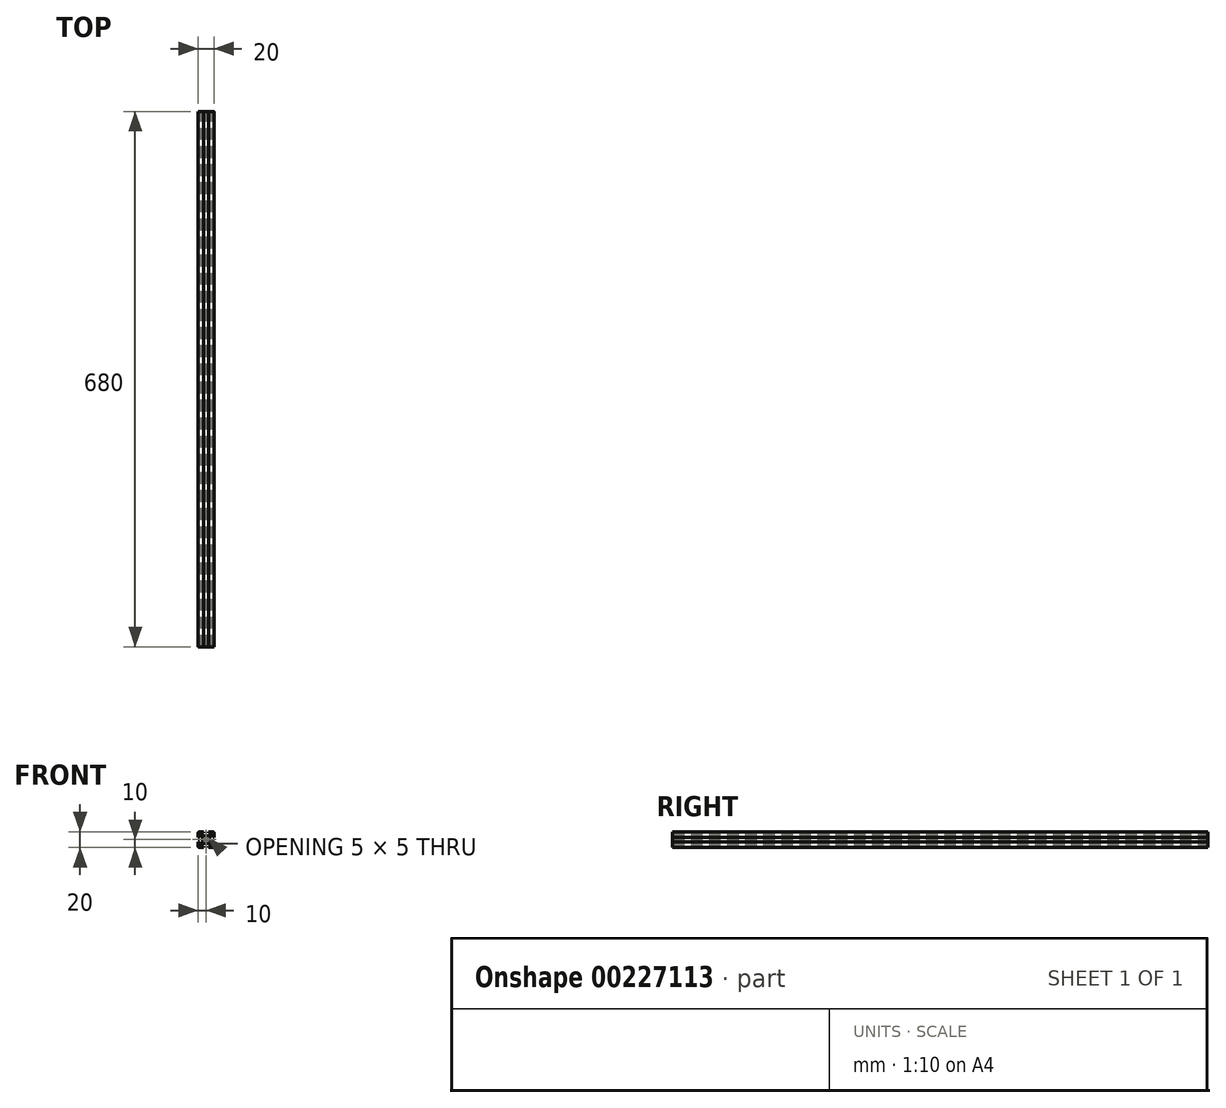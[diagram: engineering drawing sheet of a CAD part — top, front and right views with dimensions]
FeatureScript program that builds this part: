
annotation { "Feature Type Name" : "Feature", "Feature Type Description" : "" }
export const myFeature = defineFeature(function(context is Context, id is Id, definition is map)
    precondition{}
    {
        {
            var Q0;
            Q0=qCreatedBy(makeId("Front.planeOp"),FACE);
            var sketch = newSketch(context, id + "F0", { "sketchPlane" : qUnion([Q0])});
            skLineSegment(sketch, "E0.bottom", {"start": v(8.5, -10) * mm, "end": v(3, -10) * mm});
            skLineSegment(sketch, "E0.top", {"start": v(8.5, 10) * mm, "end": v(3, 10) * mm});
            skLineSegment(sketch, "E0.left", {"start": v(10, -8.5) * mm, "end": v(10, -3) * mm});
            skLineSegment(sketch, "E0.right", {"start": v(-10, -8.5) * mm, "end": v(-10, -3) * mm});
            skPoint(sketch, "E0.middle", {"position": v(0, 0) * mm});
            skLineSegment(sketch, "E1.bottom", {"start": v(6, -8.5) * mm, "end": v(3, -8.5) * mm});
            skLineSegment(sketch, "E1.top", {"start": v(6, 8.5) * mm, "end": v(3, 8.5) * mm});
            skLineSegment(sketch, "E1.left", {"start": v(8.5, -6) * mm, "end": v(8.5, -3) * mm});
            skLineSegment(sketch, "E1.right", {"start": v(-8.5, -6) * mm, "end": v(-8.5, -3) * mm});
            skLineSegment(sketch, "E2.bottom", {"start": v(3.44, -4.5) * mm, "end": v(-3.44, -4.5) * mm});
            skLineSegment(sketch, "E2.top", {"start": v(3.44, 4.5) * mm, "end": v(-3.44, 4.5) * mm});
            skLineSegment(sketch, "E2.left", {"start": v(4.5, -3.44) * mm, "end": v(4.5, 3.44) * mm});
            skLineSegment(sketch, "E2.right", {"start": v(-4.5, -3.44) * mm, "end": v(-4.5, 3.44) * mm});
            skLineSegment(sketch, "E3.bottom", {"start": v(8.5, -6) * mm, "end": v(7.06, -6) * mm});
            skLineSegment(sketch, "E3.top", {"start": v(8.5, 6) * mm, "end": v(7.06, 6) * mm});
            skLineSegment(sketch, "E4.left", {"start": v(6, -8.5) * mm, "end": v(6, -7.06) * mm});
            skLineSegment(sketch, "E4.right", {"start": v(-6, -8.5) * mm, "end": v(-6, -7.06) * mm});
            skPoint(sketch, "E5.orphan", {"position": v(-8.5, 8.5) * mm});
            skPoint(sketch, "E6.orphan", {"position": v(8.5, 8.5) * mm});
            skPoint(sketch, "E7.orphan", {"position": v(8.5, -8.5) * mm});
            skPoint(sketch, "E8.orphan", {"position": v(-8.5, -8.5) * mm});
            skLineSegment(sketch, "E9.trimOffspring", {"start": v(-6, 7.06) * mm, "end": v(-6, 8.5) * mm});
            skLineSegment(sketch, "E10.trimOffspring", {"start": v(-7.06, 6) * mm, "end": v(-8.5, 6) * mm});
            skLineSegment(sketch, "E11.trimOffspring", {"start": v(6, 7.06) * mm, "end": v(6, 8.5) * mm});
            skLineSegment(sketch, "E12.trimOffspring", {"start": v(-7.06, -6) * mm, "end": v(-8.5, -6) * mm});
            skLineSegment(sketch, "E13", {"start": v(-10, 10) * mm, "end": v(0, 0) * mm, "construction": true});
            skLineSegment(sketch, "E14", {"start": v(10, 10) * mm, "end": v(0, 0) * mm, "construction": true});
            skLineSegment(sketch, "E15", {"start": v(-6, 7.06) * mm, "end": v(-3.44, 4.5) * mm});
            skPoint(sketch, "E15.endSnap0", {"position": v(7.25, -6) * mm});
            skLineSegment(sketch, "E16", {"start": v(6, -7.06) * mm, "end": v(3.44, -4.5) * mm});
            skLineSegment(sketch, "E17", {"start": v(7.06, 6) * mm, "end": v(4.5, 3.44) * mm});
            skLineSegment(sketch, "E18", {"start": v(6, 7.06) * mm, "end": v(3.44, 4.5) * mm});
            skPoint(sketch, "E19.orphan", {"position": v(6, -6) * mm});
            skPoint(sketch, "E20.orphan", {"position": v(-4.5, -4.5) * mm});
            skPoint(sketch, "E21.orphan", {"position": v(-4.5, 4.5) * mm});
            skPoint(sketch, "E22.orphan", {"position": v(4.5, 4.5) * mm});
            skPoint(sketch, "E23.orphan", {"position": v(4.5, -4.5) * mm});
            skLineSegment(sketch, "E24.trimOffspring", {"start": v(4.5, -3.44) * mm, "end": v(7.06, -6) * mm});
            skLineSegment(sketch, "E25.trimOffspring", {"start": v(-3.44, -4.5) * mm, "end": v(-6, -7.06) * mm});
            skLineSegment(sketch, "E26.trimOffspring", {"start": v(-4.5, -3.44) * mm, "end": v(-7.06, -6) * mm});
            skLineSegment(sketch, "E27.trimOffspring", {"start": v(-4.5, 3.44) * mm, "end": v(-7.06, 6) * mm});
            skLineSegment(sketch, "E28.bottom", {"start": v(8.5, -3) * mm, "end": v(10, -3) * mm});
            skLineSegment(sketch, "E28.top", {"start": v(8.5, 3) * mm, "end": v(10, 3) * mm});
            skPoint(sketch, "E28.middle", {"position": v(10, 0) * mm});
            skLineSegment(sketch, "E29.left", {"start": v(3, 8.5) * mm, "end": v(3, 10) * mm});
            skLineSegment(sketch, "E29.right", {"start": v(-3, 8.5) * mm, "end": v(-3, 10) * mm});
            skPoint(sketch, "E29.middle", {"position": v(0, 10) * mm});
            skLineSegment(sketch, "E30.bottom", {"start": v(-8.5, 3) * mm, "end": v(-10, 3) * mm});
            skLineSegment(sketch, "E30.top", {"start": v(-8.5, -3) * mm, "end": v(-10, -3) * mm});
            skPoint(sketch, "E30.middle", {"position": v(-10, 0) * mm});
            skLineSegment(sketch, "E31.left", {"start": v(3, -8.5) * mm, "end": v(3, -10) * mm});
            skLineSegment(sketch, "E31.right", {"start": v(-3, -8.5) * mm, "end": v(-3, -10) * mm});
            skPoint(sketch, "E31.middle", {"position": v(0, -10) * mm});
            skPoint(sketch, "E32.orphan", {"position": v(3, 11.5) * mm});
            skPoint(sketch, "E33.orphan", {"position": v(-3, 11.5) * mm});
            skLineSegment(sketch, "E34.trimOffspring", {"start": v(-3, 10) * mm, "end": v(-8.5, 10) * mm});
            skLineSegment(sketch, "E35.trimOffspring", {"start": v(-3, 8.5) * mm, "end": v(-6, 8.5) * mm});
            skPoint(sketch, "E28.right.end.orphan", {"position": v(11.5, 3) * mm});
            skPoint(sketch, "E36.orphan", {"position": v(11.5, -3) * mm});
            skLineSegment(sketch, "E37.trimOffspring", {"start": v(10, 3) * mm, "end": v(10, 8.5) * mm});
            skLineSegment(sketch, "E38.trimOffspring", {"start": v(8.5, 3) * mm, "end": v(8.5, 6) * mm});
            skPoint(sketch, "E39.orphan", {"position": v(3, -11.5) * mm});
            skPoint(sketch, "E40.orphan", {"position": v(-3, -11.5) * mm});
            skLineSegment(sketch, "E41.trimOffspring", {"start": v(-3, -10) * mm, "end": v(-8.5, -10) * mm});
            skLineSegment(sketch, "E42.trimOffspring", {"start": v(-3, -8.5) * mm, "end": v(-6, -8.5) * mm});
            skPoint(sketch, "E30.right.end.orphan", {"position": v(-11.5, -3) * mm});
            skPoint(sketch, "E43.orphan", {"position": v(-11.5, 3) * mm});
            skLineSegment(sketch, "E44.trimOffspring", {"start": v(-10, 3) * mm, "end": v(-10, 8.5) * mm});
            skLineSegment(sketch, "E45.trimOffspring", {"start": v(-8.5, 3) * mm, "end": v(-8.5, 6) * mm});
            skLineSegment(sketch, "E46.trimOffspring", {"start": v(0, 0) * mm, "end": v(10, -10) * mm, "construction": true});
            skLineSegment(sketch, "E47.trimOffspring", {"start": v(0, 0) * mm, "end": v(-10, -10) * mm, "construction": true});
            skArc(sketch, "E48", {"start": v(1.16, 2.22) * mm, "mid": v(0, 2.5) * mm, "end": v(-1.16, 2.22) * mm});
            skLineSegment(sketch, "E49", {"start": v(-2.5, -1.44) * mm, "end": v(1.44, 2.5) * mm});
            skLineSegment(sketch, "E50", {"start": v(2.5, 1.44) * mm, "end": v(-1.44, -2.5) * mm});
            skLineSegment(sketch, "E51", {"start": v(1.44, -2.5) * mm, "end": v(-2.5, 1.44) * mm});
            skLineSegment(sketch, "E52", {"start": v(-1.44, 2.5) * mm, "end": v(2.5, -1.44) * mm});
            skLineSegment(sketch, "E53", {"start": v(2.5, 1.44) * mm, "end": v(2.5, -1.44) * mm, "construction": true});
            skLineSegment(sketch, "E54", {"start": v(1.44, -2.5) * mm, "end": v(-1.44, -2.5) * mm, "construction": true});
            skLineSegment(sketch, "E55", {"start": v(-2.5, -1.44) * mm, "end": v(-2.5, 1.44) * mm, "construction": true});
            skLineSegment(sketch, "E56", {"start": v(-1.44, 2.5) * mm, "end": v(1.44, 2.5) * mm, "construction": true});
            skLineSegment(sketch, "E57", {"start": v(-1.44, 2.5) * mm, "end": v(-2.5, 1.44) * mm});
            skLineSegment(sketch, "E58", {"start": v(1.44, 2.5) * mm, "end": v(2.5, 1.44) * mm});
            skLineSegment(sketch, "E59", {"start": v(2.5, -1.44) * mm, "end": v(1.44, -2.5) * mm});
            skLineSegment(sketch, "E60", {"start": v(-1.44, -2.5) * mm, "end": v(-2.5, -1.44) * mm});
            skArc(sketch, "E61.trimOffspring", {"start": v(-2.22, 1.16) * mm, "mid": v(-2.5, 0) * mm, "end": v(-2.22, -1.16) * mm});
            skArc(sketch, "E62.trimOffspring", {"start": v(-1.16, -2.22) * mm, "mid": v(0, -2.5) * mm, "end": v(1.16, -2.22) * mm});
            skArc(sketch, "E63.trimOffspring", {"start": v(2.22, -1.16) * mm, "mid": v(2.5, 0) * mm, "end": v(2.22, 1.16) * mm});
            skPoint(sketch, "E64.visualSharp", {"position": v(10, 10) * mm});
            skArc(sketch, "E64.filletArc", {"start": v(10, 8.5) * mm, "mid": v(9.56, 9.56) * mm, "end": v(8.5, 10) * mm});
            skPoint(sketch, "E65.visualSharp", {"position": v(10, -10) * mm});
            skArc(sketch, "E65.filletArc", {"start": v(8.5, -10) * mm, "mid": v(9.56, -9.56) * mm, "end": v(10, -8.5) * mm});
            skPoint(sketch, "E66.visualSharp", {"position": v(-10, -10) * mm});
            skArc(sketch, "E66.filletArc", {"start": v(-10, -8.5) * mm, "mid": v(-9.56, -9.56) * mm, "end": v(-8.5, -10) * mm});
            skPoint(sketch, "E67.visualSharp", {"position": v(-10, 10) * mm});
            skArc(sketch, "E67.filletArc", {"start": v(-8.5, 10) * mm, "mid": v(-9.56, 9.56) * mm, "end": v(-10, 8.5) * mm});
            skSolve(sketch);
        }
        {
            assignVariable(context, id + "F2", {"name" : "Length", "anyValue" : 680});
        }
        {
            var Q0;
            Q0=qSketchRegion(id+"F0",true);
            extrude(context, id + "F1", {"entities" : qUnion([Q0]), "depth" : (getVariable(context, 'Length')) * mm});
        }
    });
